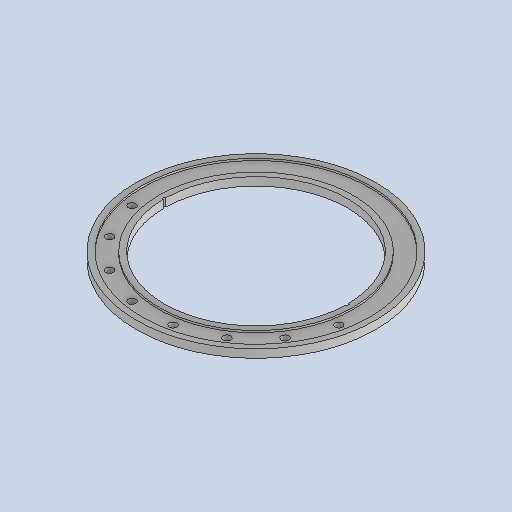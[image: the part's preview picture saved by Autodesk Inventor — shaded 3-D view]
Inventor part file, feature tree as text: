
AUTODESK INVENTOR PART (.ipt)
format: ipt  version: 2025 (Build 290162010, 162A)  size: 226,304 bytes
history: native  units: mm
features: extrude x4, sketch x4, pattern_circular x1, mirror x1, projected_geometry x1, other x1
ambient origin geometry x8: Origin, YZ Plane, XZ Plane, XY Plane, X Axis, Y Axis, Z Axis, Center Point
bodies: Solid1 (feature_tree)
feature tree (12):
  extrude  "Extrusion1"  Depth=15.0mm
  extrude  "Extrusion2"  TaperAngle=0.0deg  [1 undecoded]
  extrude  "Extrusion3"  Depth=52.0mm
  pattern_circular  "Circular Pattern2"  Count=39  [1 undecoded]
  extrude  "Extrusion4"  Depth=14.0mm
  mirror  "Mirror1"
  sketch  "Sketch1"  dims[d2=15.0mm d3=0.0mm d4=31.0mm]
  sketch  "Sketch2"  dims[d6=3.5mm d7=0.0mm d10=0.0mm d11=0.0mm]
  projected_geometry  "Projected Loop1"
  sketch  "Sketch3"  dims[d17=390.0mm d18=52.0mm d19=390.0mm]
  sketch  "Sketch5"  dims[d20=1.963495mm d21=14.0mm d22=80.0mm d23=157.5deg d34=0.0mm d35=0.0mm d36=5.0mm]
  other  "Definition1"
note: 2 required parameter values undecoded (feature->parameter linkage not recoverable at this tier; creation-order binding heuristic only, values carry confidence <= 0.55)
